# Revit family: Domotics-DomesticRanges-GEWISS-SYSTEM_DATA-PHONE_SOCKET_FRE
name_source: partatom
category: Apparecchi elettrici
revit_build: Autodesk Revit 2016 (Build: 20161004_0715(x64)
units: mm (PartAtom-declared; Revit-internal decimal feet)

## family parameters
Condiviso = Sì
Host = Superficie
Mantenere orientamento annotazione = Sì
Punto di calcolo locali = Sì
Quota connettore circolare = Usa diametro
Taglio con vuoti quando caricato = Sì
Tipo di parte = Normale

## types (2) — shared parameters
Carico apparente = 0 VA
Catalogue = DOMOTICS
Catalogue Range = SYSTEM - DOMESTIC RANGE
Connection = Screw-on terminals
Description. = Connector
Description: = French 8 contacts
Electrocod = 3722
IDF = c6a26cf8-1e3b-4e8a-9b07-35d354d93641
IDT = 5c633a00-f518-4a25-9df9-c437490694e6
Immagine tipo = GW21235.jpg
N. poli = 1
No. SYSTEM modules = 1
Produttore = GEWISS S.p.A.
Prospetto di default = 1219 mm
SEO = Connector
Standard: = French
Technical sheet = https://www.gewiss.com
Tipo_ = SYSTEM PRESE TEL FRA_GENERICO : GW21235
URL = https://www.gewiss.com
Version file RFA = 19.4
Volt = 230 V

## per-type parameters (varying)
| type | Colour | Descrizione | EAN code | Modello |
| GW21235 - FRENCH PHONE S.-OUTLET 8 CONTACTS SY/BK | Black | FRENCH PHONE S.-OUTLET 8 CONTACTS SY/BK | 8011564128828 | GW21235 |
| GW20235 - FRENCH PHONE S.-OUTLET 8 CONTACTS SY/WT | White | FRENCH PHONE S.-OUTLET 8 CONTACTS SY/WT | 8011564000773 | GW20235 |

## geometry (parser evidence)
native form markers: Sweep x1
no freeform markers — native parametric forms only
